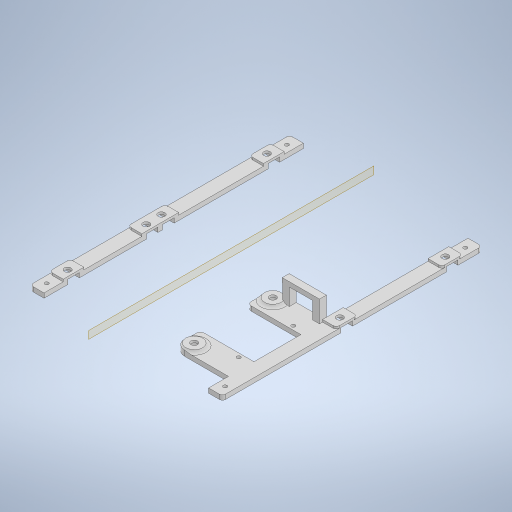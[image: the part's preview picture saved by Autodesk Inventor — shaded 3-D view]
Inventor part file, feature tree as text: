
AUTODESK INVENTOR PART (.ipt)
format: ipt  version: 2023 (Build 270158000, 158)  size: 614,400 bytes
history: native  units: mm
features: extrude x12, sketch x11, other x6, fillet x3, mirror x1, hole x1
ambient origin geometry x8: Origin, YZ Plane, XZ Plane, XY Plane, X Axis, Y Axis, Z Axis, Center Point
bodies: Body1 (feature_tree), Body2 (feature_tree)
feature tree (34):
  other  "ソリッド1"
  extrude  "押し出し1"  Depth=6.0mm
  extrude  "押し出し2"  Depth=2.4mm
  extrude  "押し出し3"  Depth=2.4mm
  other  "作業平面1"
  mirror  "ミラー1"
  extrude  "押し出し4"  Depth=1.2mm
  extrude  "押し出し5"  Depth=55.0mm
  extrude  "押し出し6"  Depth=10.0mm
  sketch  "スケッチ7"
  extrude  "押し出し7"  Depth=7.2mm TaperAngle=0.0deg
  extrude  "押し出し8"  Depth=3.5mm
  extrude  "押し出し10"  TaperAngle=0.0deg  [1 undecoded]
  sketch  "スケッチ9"
  hole  "穴1"  [1 undecoded]
  extrude  "押し出し11"  TaperAngle=0.0deg  [1 undecoded]
  extrude  "押し出し12"  Depth=46.5mm
  extrude  "押し出し13"  Depth=8.4mm
  fillet  "フィレット1"  Radius=2.4mm
  fillet  "フィレット2"  Radius=2.4mm
  fillet  "フィレット3"  Radius=41.0mm
  other  "作業平面2"
  other  "分割2"
  sketch  "スケッチ1"
  sketch  "スケッチ2"
  sketch  "スケッチ3"
  sketch  "スケッチ4"
  sketch  "スケッチ5"
  sketch  "スケッチ6"
  sketch  "スケッチ8"
  sketch  "スケッチ10"
  sketch  "スケッチ11"
  other  "ソリッド4"
  other  "ソリッド5"
note: 3 required parameter values undecoded (feature->parameter linkage not recoverable at this tier; creation-order binding heuristic only, values carry confidence <= 0.55)
